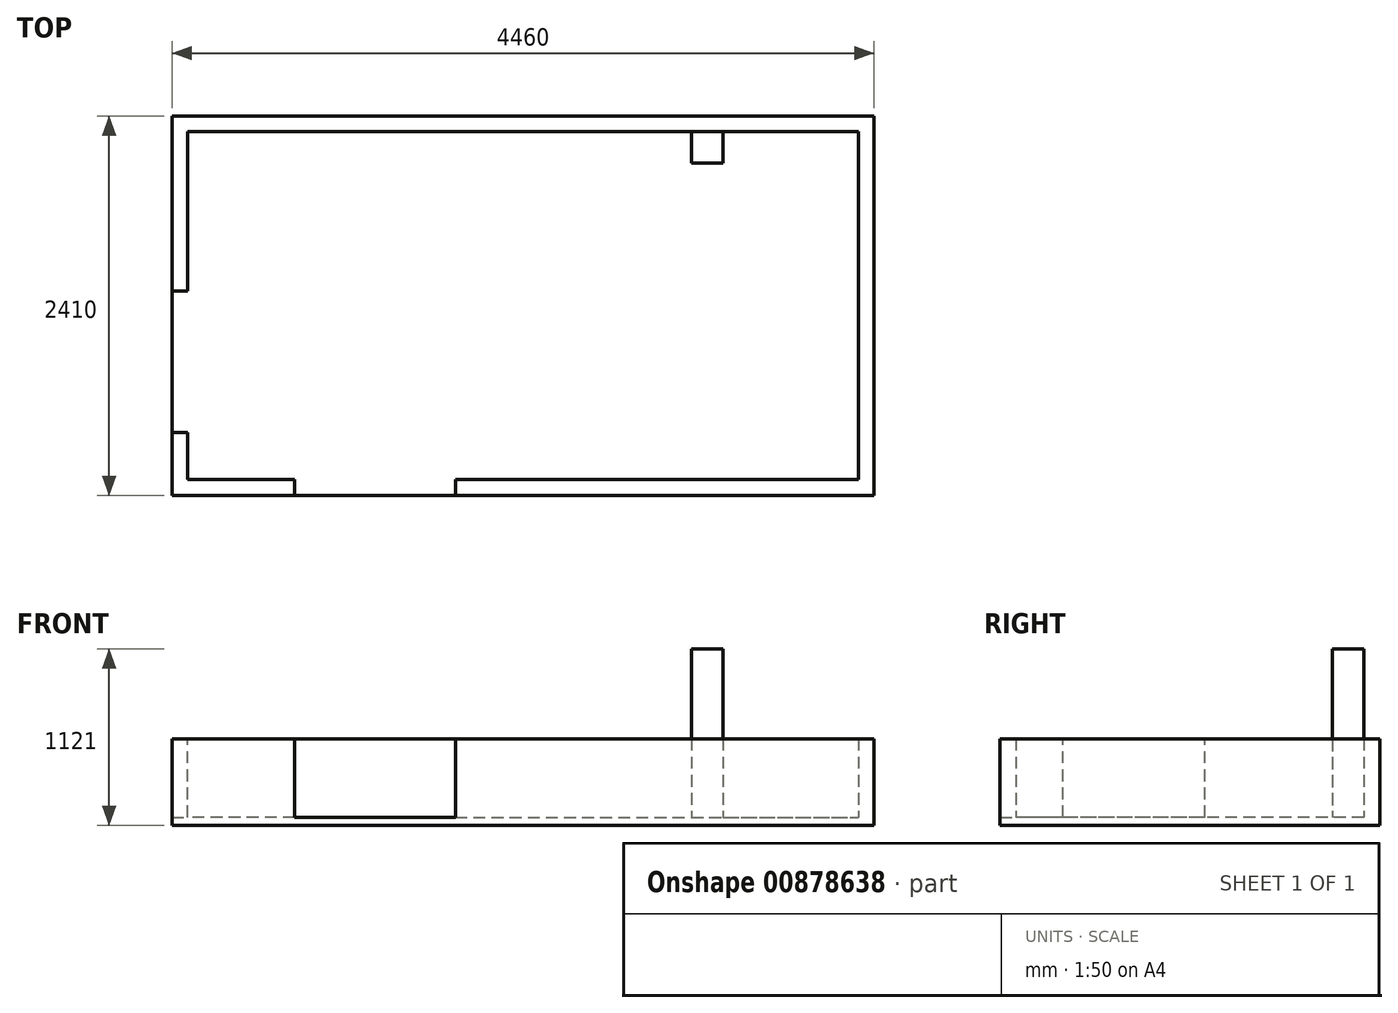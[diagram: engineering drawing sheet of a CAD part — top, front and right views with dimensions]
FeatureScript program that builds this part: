
annotation { "Feature Type Name" : "Feature", "Feature Type Description" : "" }
export const myFeature = defineFeature(function(context is Context, id is Id, definition is map)
    precondition{}
    {
        {
            var Q0;
            Q0=qCreatedBy(makeId("Top.planeOp"),FACE);
            var sketch = newSketch(context, id + "F0", { "sketchPlane" : qUnion([Q0])});
            skLineSegment(sketch, "E0.bottom", {"start": v(-2230, 1205) * mm, "end": v(2230, 1205) * mm});
            skLineSegment(sketch, "E0.top", {"start": v(-2230, -1205) * mm, "end": v(2230, -1205) * mm});
            skLineSegment(sketch, "E0.left", {"start": v(-2230, 1205) * mm, "end": v(-2230, -1205) * mm});
            skLineSegment(sketch, "E0.right", {"start": v(2230, 1205) * mm, "end": v(2230, -1205) * mm});
            skPoint(sketch, "E0.middle", {"position": v(0, 0) * mm});
            skLineSegment(sketch, "E1.left", {"start": v(-2130, 1105) * mm, "end": v(-2130, -1105) * mm});
            skLineSegment(sketch, "E1.right", {"start": v(2130, 1105) * mm, "end": v(2130, -1105) * mm});
            skLineSegment(sketch, "E2", {"start": v(-1450, -1205) * mm, "end": v(-1450, -1105) * mm});
            skLineSegment(sketch, "E3", {"start": v(-430, -1105) * mm, "end": v(-430, -1205) * mm});
            skLineSegment(sketch, "E4", {"start": v(-1450, -1105) * mm, "end": v(-2130, -1105) * mm});
            skLineSegment(sketch, "E5", {"start": v(-430, -1105) * mm, "end": v(2130, -1105) * mm});
            skLineSegment(sketch, "E6.top", {"start": v(1070, 905) * mm, "end": v(1270, 905) * mm});
            skLineSegment(sketch, "E6.left", {"start": v(1070, 1105) * mm, "end": v(1070, 905) * mm});
            skLineSegment(sketch, "E6.right", {"start": v(1270, 1105) * mm, "end": v(1270, 905) * mm});
            skLineSegment(sketch, "E7", {"start": v(-2130, 1105) * mm, "end": v(1070, 1105) * mm});
            skLineSegment(sketch, "E8", {"start": v(1270, 1105) * mm, "end": v(2130, 1105) * mm});
            skSolve(sketch);
        }
        {
            var Q0;
            Q0=makeQuery(id+"F0.imprint","IMPRINT",FACE,{"disambiguationData":[TD([[makeQuery(id+"F0.imprint","IMPRINT",EDGE,{"derivedFrom":sQuery(id+"F0.wireOp",EDGE,"E0.bottom")}),-1.0]])]});
            extrude(context, id + "F1", {"entities" : qUnion([Q0]), "depth" : 500 * mm, "offsetDistance" : 25 * mm});
        }
        {
            var Q0;
            Q0=qSketchRegion(id+"F0",true);
            extrude(context, id + "F2", {"entities" : qUnion([Q0]), "operationType" : NewBodyOperationType.ADD, "oppositeDirection" : true, "depth" : 51 * mm, "offsetDistance" : 25 * mm});
        }
        {
            var Q0;
            Q0=makeQuery(id+"F1.opExtrude","SWEPT_FACE",FACE,{"disambiguationData":[OSD([sQuery(id+"F0.wireOp",EDGE,"E1.left")])]});
            var sketch = newSketch(context, id + "F3", { "sketchPlane" : qUnion([Q0])});
            skLineSegment(sketch, "E9.bottom", {"start": v(-805, 0) * mm, "end": v(95, 0) * mm});
            skLineSegment(sketch, "E9.top", {"start": v(-805, 500) * mm, "end": v(95, 500) * mm});
            skLineSegment(sketch, "E9.left", {"start": v(-805, 0) * mm, "end": v(-805, 500) * mm});
            skLineSegment(sketch, "E9.right", {"start": v(95, 0) * mm, "end": v(95, 500) * mm});
            skSolve(sketch);
        }
        {
            var Q0;
            Q0=qSketchRegion(id+"F3",true);
            extrude(context, id + "F4", {"entities" : qUnion([Q0]), "operationType" : NewBodyOperationType.REMOVE, "oppositeDirection" : true, "depth" : 190 * mm, "offsetDistance" : 25 * mm});
        }
        {
            var Q0;
            {var subQ0=sQuery(id+"F0.wireOp",EDGE,"E6.top");var subQ1=sQuery(id+"F0.wireOp",EDGE,"E0.left");var subQ2=sQuery(id+"F0.wireOp",EDGE,"E5");var subQ3=sQuery(id+"F0.wireOp",EDGE,"E0.top");var subQ4=sQuery(id+"F0.wireOp",EDGE,"E3");var subQ5=sQuery(id+"F0.wireOp",EDGE,"E1.right");var subQ6=sQuery(id+"F0.wireOp",EDGE,"E1.left");var subQ7=sQuery(id+"F0.wireOp",EDGE,"E0.right");var subQ8=sQuery(id+"F0.wireOp",EDGE,"E0.bottom");var subQ9=sQuery(id+"F0.wireOp",EDGE,"E2");var subQ10=sQuery(id+"F0.wireOp",EDGE,"E6.left");var subQ11=sQuery(id+"F0.wireOp",EDGE,"E6.right");var subQ12=sQuery(id+"F0.wireOp",EDGE,"E7");var subQ13=sQuery(id+"F0.wireOp",EDGE,"E8");Q0=makeQuery(id+"F4.boolean.opBoolean","SPLIT",FACE,{"disambiguationData":[TD([makeQuery(id+"F1.opExtrude","SWEPT_FACE",FACE,{"disambiguationData":[OSD([subQ8])]})])],"derivedFrom":makeQuery(id+"F1.opExtrude","CAP_FACE",FACE,{"disambiguationData":[OSD([subQ8,subQ3,subQ1,subQ7,subQ6,subQ5,subQ9,subQ4,sQuery(id+"F0.wireOp",EDGE,"E4"),subQ2,subQ0,subQ10,subQ11,subQ12,subQ13])],"isStart":false})});}
            var sketch = newSketch(context, id + "F5", { "sketchPlane" : qUnion([Q0])});
            skLineSegment(sketch, "E10.bottom", {"start": v(1270, 905) * mm, "end": v(1070, 905) * mm});
            skLineSegment(sketch, "E10.top", {"start": v(1270, 1105) * mm, "end": v(1070, 1105) * mm});
            skLineSegment(sketch, "E10.left", {"start": v(1270, 905) * mm, "end": v(1270, 1105) * mm});
            skLineSegment(sketch, "E10.right", {"start": v(1070, 905) * mm, "end": v(1070, 1105) * mm});
            skSolve(sketch);
        }
        {
            var Q0;
            Q0=qSketchRegion(id+"F5",true);
            extrude(context, id + "F6", {"entities" : qUnion([Q0]), "operationType" : NewBodyOperationType.ADD, "depth" : 570 * mm, "offsetDistance" : 25 * mm});
        }
    });
